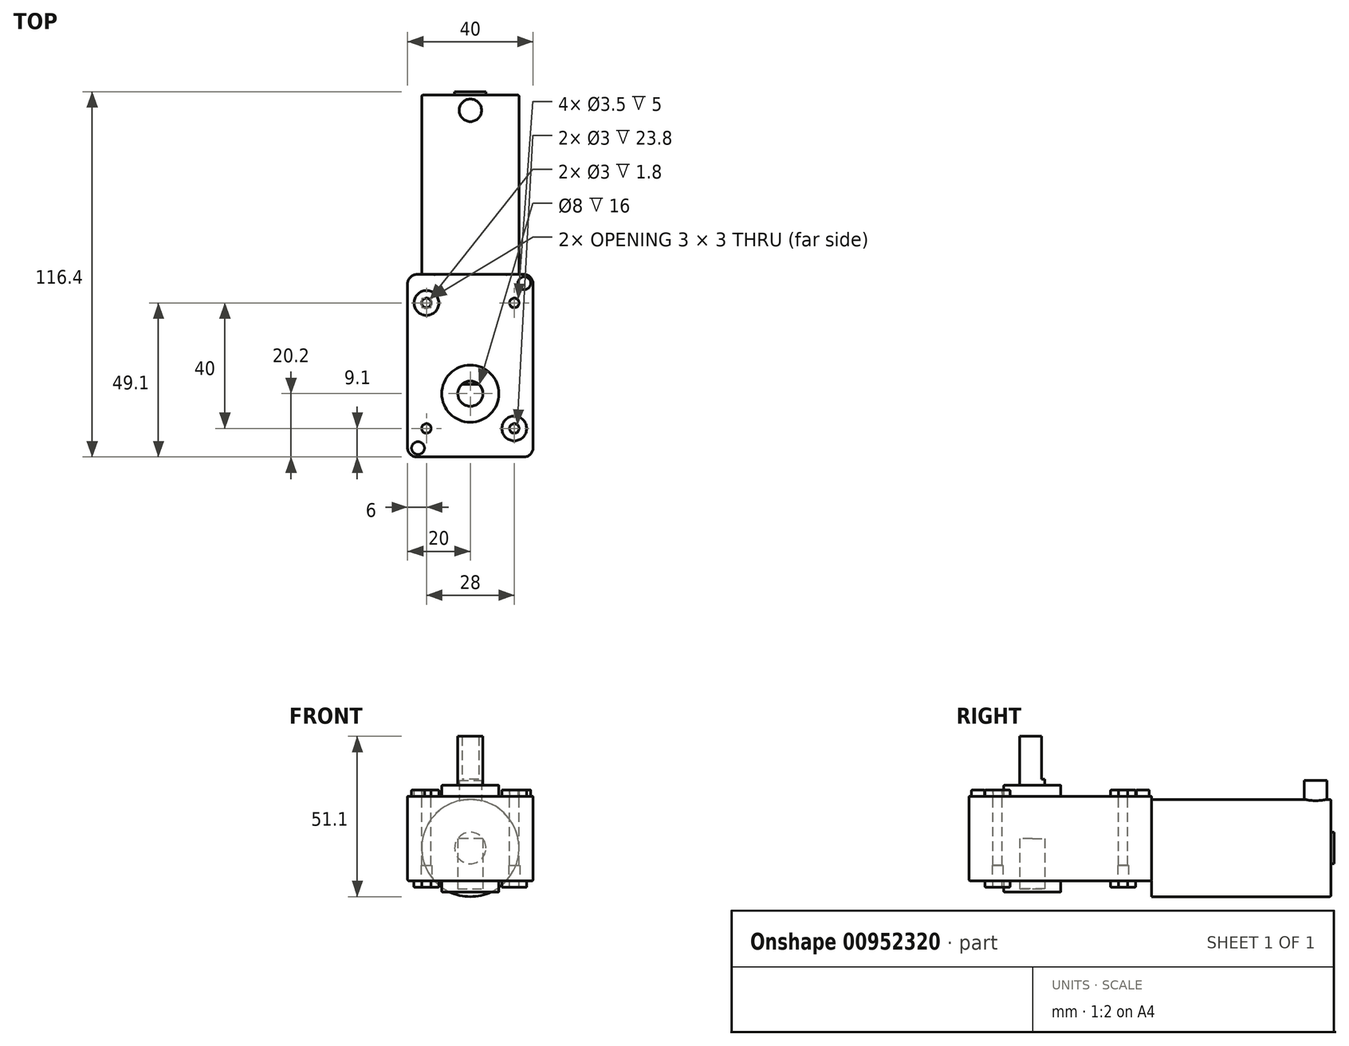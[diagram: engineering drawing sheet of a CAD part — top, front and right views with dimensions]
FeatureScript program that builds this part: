
annotation { "Feature Type Name" : "Feature", "Feature Type Description" : "" }
export const myFeature = defineFeature(function(context is Context, id is Id, definition is map)
    precondition{}
    {
        {
            var Q0;
            Q0=qCreatedBy(makeId("Top.planeOp"),FACE);
            var sketch = newSketch(context, id + "F0", { "sketchPlane" : qUnion([Q0])});
            skLineSegment(sketch, "E0.bottom", {"start": v(20, -29.1) * mm, "end": v(-20, -29.1) * mm});
            skLineSegment(sketch, "E0.top", {"start": v(20, 29.1) * mm, "end": v(-20, 29.1) * mm});
            skLineSegment(sketch, "E0.left", {"start": v(20, -29.1) * mm, "end": v(20, 29.1) * mm});
            skLineSegment(sketch, "E0.right", {"start": v(-20, -29.1) * mm, "end": v(-20, 29.1) * mm});
            skPoint(sketch, "E0.middle", {"position": v(0, 0) * mm});
            skCircle(sketch, "E1", {"center": v(0, -8.9) * mm, "radius": 4 * mm});
            skCircle(sketch, "E2", {"center": v(0, -8.9) * mm, "radius": 9.1 * mm});
            skSolve(sketch);
        }
        {
            var Q0;
            Q0=qSketchRegion(id+"F0",true);
            extrude(context, id + "F1", {"entities" : qUnion([Q0]), "depth" : 27 * mm, "offsetDistance" : 25 * mm, "symmetric" : true});
        }
        {
            var Q0;
            Q0=makeQuery(id+"F0.imprint","IMPRINT",FACE,{"disambiguationData":[TD([[makeQuery(id+"F0.imprint","IMPRINT",EDGE,{"derivedFrom":sQuery(id+"F0.wireOp",EDGE,"E1")}),-1.0]])]});
            extrude(context, id + "F2", {"entities" : qUnion([Q0]), "operationType" : NewBodyOperationType.ADD, "depth" : 34 * mm, "offsetDistance" : 25 * mm, "symmetric" : true});
        }
        {
            var Q0;
            Q0=makeQuery(id+"F6.imprint","IMPRINT",FACE,{"disambiguationData":[TD([[makeQuery(id+"F6.imprint","IMPRINT",EDGE,{"derivedFrom":sQuery(id+"F6.wireOp",EDGE,"KXEyg77E-2VgL-bzDm-OMNw-jEKFs803UJ2D")}),1.0]])]});
            var Q1;
            Q1=makeQuery(id+"F0.imprint","IMPRINT",FACE,{"disambiguationData":[TD([[makeQuery(id+"F0.imprint","IMPRINT",EDGE,{"derivedFrom":sQuery(id+"F0.wireOp",EDGE,"E1")}),1.0]])]});
            extrude(context, id + "F3", {"entities" : qUnion([Q0, Q1]), "operationType" : NewBodyOperationType.ADD, "depth" : 32.6 * mm, "offsetDistance" : 25 * mm});
        }
        {
            var Q0;
            Q0=makeQuery(id+"F1.opExtrude","SWEPT_FACE",FACE,{"disambiguationData":[OSD([sQuery(id+"F0.wireOp",EDGE,"E0.top")])]});
            var sketch = newSketch(context, id + "F4", { "sketchPlane" : qUnion([Q0])});
            skCircle(sketch, "E3", {"center": v(0, -3) * mm, "radius": 15.5 * mm});
            skSolve(sketch);
        }
        {
            var Q0;
            {var subQ0=sQuery(id+"F4.wireOp",EDGE,"E3");var subQ1=makeQuery(id+"F1.opExtrude","CAP_EDGE",EDGE,{"disambiguationData":[OSD([sQuery(id+"F0.wireOp",EDGE,"E0.top")])],"isStart":true});var subQ2=makeQuery(id+"F4.imprint","INTERSECT",VERTEX,{"disambiguationData":[OD(0.0)],"derivedFrom":[subQ1,subQ0]});Q0=makeQuery(id+"F4.imprint","IMPRINT",FACE,{"disambiguationData":[TD([[makeQuery(id+"F4.imprint","IMPRINT",EDGE,{"disambiguationData":[TD([[subQ2,-1.0]])],"derivedFrom":subQ0}),1.0]])]});}
            var Q1;
            {var subQ0=sQuery(id+"F4.wireOp",EDGE,"E3");var subQ1=sQuery(id+"F0.wireOp",EDGE,"E0.top");var subQ2=makeQuery(id+"F1.opExtrude","CAP_EDGE",EDGE,{"disambiguationData":[OSD([subQ1])],"isStart":true});var subQ3=makeQuery(id+"F4.imprint","INTERSECT",VERTEX,{"disambiguationData":[OD(0.0)],"derivedFrom":[subQ2,subQ0]});Q1=makeQuery(id+"F4.imprint","IMPRINT",FACE,{"disambiguationData":[TD([[makeQuery(id+"F4.imprint","IMPRINT",EDGE,{"disambiguationData":[TD([[subQ3,1.0]])],"derivedFrom":subQ0}),1.0]])]});}
            extrude(context, id + "F5", {"entities" : qUnion([Q0, Q1]), "operationType" : NewBodyOperationType.ADD, "depth" : 57.2 * mm, "offsetDistance" : 25 * mm});
        }
        {
            var Q0;
            Q0=makeQuery(id+"F1.opExtrude","CAP_FACE",FACE,{"disambiguationData":[OSD([sQuery(id+"F0.wireOp",EDGE,"E0.bottom"),sQuery(id+"F0.wireOp",EDGE,"E0.top"),sQuery(id+"F0.wireOp",EDGE,"E0.left"),sQuery(id+"F0.wireOp",EDGE,"E0.right")])],"isStart":false});
            var sketch = newSketch(context, id + "F6", { "sketchPlane" : qUnion([Q0])});
            skCircle(sketch, "E4", {"center": v(-14, 20) * mm, "radius": 1.5 * mm});
            skCircle(sketch, "E5.MirrorC", {"center": v(14, 20) * mm, "radius": 1.5 * mm});
            skCircle(sketch, "E6.MirrorC", {"center": v(-14, -20) * mm, "radius": 1.5 * mm});
            skCircle(sketch, "E7.MirrorC", {"center": v(14, -20) * mm, "radius": 1.5 * mm});
            skCircle(sketch, "E8", {"center": v(-14, 20) * mm, "radius": 3.95 * mm});
            skArc(sketch, "E9.MirrorC", {"start": v(11.3, 22.89) * mm, "mid": v(16.89, 22.7) * mm, "end": v(16.7, 17.11) * mm});
            skCircle(sketch, "E10.MirrorC", {"center": v(-14, -20) * mm, "radius": 3.95 * mm});
            skCircle(sketch, "E11.MirrorC", {"center": v(14, -20) * mm, "radius": 3.95 * mm});
            skCircle(sketch, "E12", {"center": v(0, -8.9) * mm, "radius": 6.39 * mm});
            skArc(sketch, "E13", {"start": v(4.87, 16.88) * mm, "mid": v(4.68, 11.3) * mm, "end": v(10.26, 11.1) * mm});
            skLineSegment(sketch, "E14", {"start": v(16.7, 17.11) * mm, "end": v(10.26, 11.1) * mm});
            skLineSegment(sketch, "E15.MirrorCS", {"start": v(11.3, 22.89) * mm, "end": v(4.87, 16.88) * mm});
            skCircle(sketch, "E16", {"center": v(17.2, 26.3) * mm, "radius": 2.05 * mm});
            skLineSegment(sketch, "E17", {"start": v(20, 0) * mm, "end": v(19.1, 0) * mm});
            skLineSegment(sketch, "E18", {"start": v(0, -29.1) * mm, "end": v(0, -27.97) * mm});
            skCircle(sketch, "E19.MirrorC", {"center": v(16.67, -26.24) * mm, "radius": 2.05 * mm});
            skCircle(sketch, "E20.MirrorC", {"center": v(-16.67, -26.24) * mm, "radius": 2.05 * mm});
            skCircle(sketch, "E21.MirrorC", {"center": v(-17.2, 26.3) * mm, "radius": 2.05 * mm});
            skSolve(sketch);
        }
        {
            var Q0;
            Q0=makeQuery(id+"F3.opExtrude","CAP_FACE",FACE,{"disambiguationData":[OSD([sQuery(id+"F0.wireOp",EDGE,"E1")])],"isStart":false});
            var sketch = newSketch(context, id + "F7", { "sketchPlane" : qUnion([Q0])});
            skLineSegment(sketch, "E22.bottom", {"start": v(5, -5.9) * mm, "end": v(-5, -5.9) * mm});
            skLineSegment(sketch, "E22.top", {"start": v(5, -3.9) * mm, "end": v(-5, -3.9) * mm});
            skLineSegment(sketch, "E22.left", {"start": v(5, -5.9) * mm, "end": v(5, -3.9) * mm});
            skLineSegment(sketch, "E22.right", {"start": v(-5, -5.9) * mm, "end": v(-5, -3.9) * mm});
            skPoint(sketch, "E22.middle", {"position": v(0, -4.9) * mm});
            skCircle(sketch, "E23", {"center": v(0, -8.9) * mm, "radius": 4 * mm});
            skSolve(sketch);
        }
        {
            var Q0;
            Q0=makeQuery(id+"F7.imprint","IMPRINT",FACE,{"disambiguationData":[TD([[makeQuery(id+"F7.imprint","IMPRINT",EDGE,{"derivedFrom":sQuery(id+"F7.wireOp",EDGE,"E22.top")}),1.0]])]});
            var Q1;
            {var subQ0=sQuery(id+"F7.wireOp",EDGE,"E23");var subQ1=sQuery(id+"F7.wireOp",EDGE,"E22.bottom");var subQ2=makeQuery(id+"F7.imprint","INTERSECT",VERTEX,{"disambiguationData":[OD(0.0)],"derivedFrom":[subQ1,subQ0]});Q1=makeQuery(id+"F7.imprint","IMPRINT",FACE,{"disambiguationData":[TD([[makeQuery(id+"F7.imprint","IMPRINT",EDGE,{"disambiguationData":[TD([[subQ2,-1.0]])],"derivedFrom":subQ1}),-1.0]])]});}
            extrude(context, id + "F8", {"entities" : qUnion([Q0, Q1]), "operationType" : NewBodyOperationType.REMOVE, "oppositeDirection" : true, "depth" : 13.7 * mm, "offsetDistance" : 25 * mm});
        }
        {
            var Q0;
            Q0=makeQuery(id+"F6.imprint","IMPRINT",FACE,{"disambiguationData":[TD([[makeQuery(id+"F6.imprint","IMPRINT",EDGE,{"derivedFrom":sQuery(id+"F6.wireOp",EDGE,"E5.MirrorC")}),1.0]])]});
            var Q1;
            Q1=makeQuery(id+"F6.imprint","IMPRINT",FACE,{"disambiguationData":[TD([[makeQuery(id+"F6.imprint","IMPRINT",EDGE,{"derivedFrom":sQuery(id+"F6.wireOp",EDGE,"E6.MirrorC")}),1.0]])]});
            var Q2;
            Q2=makeQuery(id+"F6.imprint","IMPRINT",FACE,{"disambiguationData":[TD([[makeQuery(id+"F6.imprint","IMPRINT",EDGE,{"derivedFrom":sQuery(id+"F6.wireOp",EDGE,"E7.MirrorC")}),-1.0]])]});
            var Q3;
            Q3=makeQuery(id+"F6.imprint","IMPRINT",FACE,{"disambiguationData":[TD([[makeQuery(id+"F6.imprint","IMPRINT",EDGE,{"derivedFrom":sQuery(id+"F6.wireOp",EDGE,"E4")}),-1.0]])]});
            extrude(context, id + "F9", {"entities" : qUnion([Q0, Q1, Q2, Q3]), "operationType" : NewBodyOperationType.ADD, "oppositeDirection" : true, "depth" : 29 * mm, "offsetDistance" : 25 * mm});
        }
        {
            var Q0;
            Q0=makeQuery(id+"F6.imprint","IMPRINT",FACE,{"disambiguationData":[TD([[makeQuery(id+"F6.imprint","IMPRINT",EDGE,{"derivedFrom":sQuery(id+"F6.wireOp",EDGE,"E4")}),-1.0]])]});
            var Q1;
            Q1=makeQuery(id+"F6.imprint","IMPRINT",FACE,{"disambiguationData":[TD([[makeQuery(id+"F6.imprint","IMPRINT",EDGE,{"derivedFrom":sQuery(id+"F6.wireOp",EDGE,"E5.MirrorC")}),1.0]])]});
            var Q2;
            Q2=makeQuery(id+"F6.imprint","IMPRINT",FACE,{"disambiguationData":[TD([[makeQuery(id+"F6.imprint","IMPRINT",EDGE,{"derivedFrom":sQuery(id+"F6.wireOp",EDGE,"E6.MirrorC")}),1.0]])]});
            var Q3;
            Q3=makeQuery(id+"F6.imprint","IMPRINT",FACE,{"disambiguationData":[TD([[makeQuery(id+"F6.imprint","IMPRINT",EDGE,{"derivedFrom":sQuery(id+"F6.wireOp",EDGE,"E7.MirrorC")}),-1.0]])]});
            var Q4;
            Q4=makeQuery(id+"F6.imprint","IMPRINT",FACE,{"disambiguationData":[TD([[makeQuery(id+"F6.imprint","IMPRINT",EDGE,{"derivedFrom":sQuery(id+"F6.wireOp",EDGE,"E16")}),1.0]])]});
            var Q5;
            Q5=makeQuery(id+"F6.imprint","IMPRINT",FACE,{"disambiguationData":[TD([[makeQuery(id+"F6.imprint","IMPRINT",EDGE,{"derivedFrom":sQuery(id+"F6.wireOp",EDGE,"E21.MirrorC")}),-1.0]])]});
            var Q6;
            Q6=makeQuery(id+"F6.imprint","IMPRINT",FACE,{"disambiguationData":[TD([[makeQuery(id+"F6.imprint","IMPRINT",EDGE,{"derivedFrom":sQuery(id+"F6.wireOp",EDGE,"E20.MirrorC")}),1.0]])]});
            var Q7;
            Q7=makeQuery(id+"F6.imprint","IMPRINT",FACE,{"disambiguationData":[TD([[makeQuery(id+"F6.imprint","IMPRINT",EDGE,{"derivedFrom":sQuery(id+"F6.wireOp",EDGE,"E19.MirrorC")}),-1.0]])]});
            extrude(context, id + "F10", {"entities" : qUnion([Q0, Q1, Q2, Q3, Q4, Q5, Q6, Q7]), "operationType" : NewBodyOperationType.ADD, "depth" : 2 * mm, "offsetDistance" : 25 * mm});
        }
        {
            var Q0;
            Q0=makeQuery(id+"F10.boolean.opBoolean","SPLIT",FACE,{"disambiguationData":[TD([makeQuery(id+"F10.opExtrude","SWEPT_FACE",FACE,{"disambiguationData":[OSD([sQuery(id+"F6.wireOp",EDGE,"E4")])]})])],"derivedFrom":makeQuery(id+"F1.opExtrude","CAP_FACE",FACE,{"disambiguationData":[OSD([sQuery(id+"F0.wireOp",EDGE,"E0.bottom"),sQuery(id+"F0.wireOp",EDGE,"E0.top"),sQuery(id+"F0.wireOp",EDGE,"E0.left"),sQuery(id+"F0.wireOp",EDGE,"E0.right"),sQuery(id+"F0.wireOp",EDGE,"E2")])],"isStart":false})});
            var Q1;
            Q1=makeQuery(id+"F10.boolean.opBoolean","SPLIT",FACE,{"disambiguationData":[TD([makeQuery(id+"F10.opExtrude","SWEPT_FACE",FACE,{"disambiguationData":[OSD([sQuery(id+"F6.wireOp",EDGE,"E5.MirrorC")])]})])],"derivedFrom":makeQuery(id+"F1.opExtrude","CAP_FACE",FACE,{"disambiguationData":[OSD([sQuery(id+"F0.wireOp",EDGE,"E0.bottom"),sQuery(id+"F0.wireOp",EDGE,"E0.top"),sQuery(id+"F0.wireOp",EDGE,"E0.left"),sQuery(id+"F0.wireOp",EDGE,"E0.right"),sQuery(id+"F0.wireOp",EDGE,"E2")])],"isStart":false})});
            var Q2;
            Q2=makeQuery(id+"F10.boolean.opBoolean","SPLIT",FACE,{"disambiguationData":[TD([makeQuery(id+"F10.opExtrude","SWEPT_FACE",FACE,{"disambiguationData":[OSD([sQuery(id+"F6.wireOp",EDGE,"E6.MirrorC")])]})])],"derivedFrom":makeQuery(id+"F1.opExtrude","CAP_FACE",FACE,{"disambiguationData":[OSD([sQuery(id+"F0.wireOp",EDGE,"E0.bottom"),sQuery(id+"F0.wireOp",EDGE,"E0.top"),sQuery(id+"F0.wireOp",EDGE,"E0.left"),sQuery(id+"F0.wireOp",EDGE,"E0.right"),sQuery(id+"F0.wireOp",EDGE,"E2")])],"isStart":false})});
            var Q3;
            Q3=makeQuery(id+"F10.boolean.opBoolean","SPLIT",FACE,{"disambiguationData":[TD([makeQuery(id+"F10.opExtrude","SWEPT_FACE",FACE,{"disambiguationData":[OSD([sQuery(id+"F6.wireOp",EDGE,"E7.MirrorC")])]})])],"derivedFrom":makeQuery(id+"F1.opExtrude","CAP_FACE",FACE,{"disambiguationData":[OSD([sQuery(id+"F0.wireOp",EDGE,"E0.bottom"),sQuery(id+"F0.wireOp",EDGE,"E0.top"),sQuery(id+"F0.wireOp",EDGE,"E0.left"),sQuery(id+"F0.wireOp",EDGE,"E0.right"),sQuery(id+"F0.wireOp",EDGE,"E2")])],"isStart":false})});
            extrude(context, id + "F11", {"entities" : qUnion([Q0, Q1, Q2, Q3]), "operationType" : NewBodyOperationType.REMOVE, "endBound" : BoundingType.THROUGH_ALL, "oppositeDirection" : true, "depth" : 25 * mm, "offsetDistance" : 25 * mm});
        }
        {
            var Q0;
            Q0=makeQuery(id+"F5.opExtrude","CAP_FACE",FACE,{"disambiguationData":[OSD([sQuery(id+"F4.wireOp",EDGE,"E3")])],"isStart":false});
            var sketch = newSketch(context, id + "F12", { "sketchPlane" : qUnion([Q0])});
            skCircle(sketch, "E24", {"center": v(0, -3) * mm, "radius": 5 * mm});
            skSolve(sketch);
        }
        {
            var Q0;
            Q0=qSketchRegion(id+"F12",true);
            extrude(context, id + "F13", {"entities" : qUnion([Q0]), "operationType" : NewBodyOperationType.ADD, "depth" : 1 * mm, "offsetDistance" : 25 * mm});
        }
        {
            var Q0;
            {var subQ0=sQuery(id+"F0.wireOp",EDGE,"E0.left");var subQ1=sQuery(id+"F0.wireOp",EDGE,"E0.top");var subQ2=sQuery(id+"F0.wireOp",EDGE,"E0.right");var subQ3=sQuery(id+"F0.wireOp",EDGE,"E0.bottom");var subQ4=sQuery(id+"F0.wireOp",EDGE,"E2");Q0=makeQuery(id+"F10.boolean.opBoolean","SPLIT",FACE,{"disambiguationData":[TD([makeQuery(id+"F1.opExtrude","SWEPT_FACE",FACE,{"disambiguationData":[OSD([subQ3])]})])],"derivedFrom":makeQuery(id+"F1.opExtrude","CAP_FACE",FACE,{"disambiguationData":[OSD([subQ3,subQ1,subQ0,subQ2,subQ4])],"isStart":false})});}
            var sketch = newSketch(context, id + "F14", { "sketchPlane" : qUnion([Q0])});
            skCircle(sketch, "E25", {"center": v(0, 81.39) * mm, "radius": 3.59 * mm});
            skSolve(sketch);
        }
        {
            var Q0;
            Q0=makeQuery(id+"F14.imprint","IMPRINT",FACE,{"disambiguationData":[TD([[makeQuery(id+"F14.imprint","IMPRINT",EDGE,{"derivedFrom":sQuery(id+"F14.wireOp",EDGE,"E25")}),1.0]])]});
            extrude(context, id + "F15", {"entities" : qUnion([Q0]), "operationType" : NewBodyOperationType.ADD, "depth" : 10 * mm, "offsetDistance" : 25 * mm, "symmetric" : true});
        }
        {
            var Q0;
            Q0=makeQuery(id+"F1.opExtrude","SWEPT_EDGE",EDGE,{"disambiguationData":[OSD([sQuery(id+"F0.wireOp",EDGE,"E0.top"),sQuery(id+"F0.wireOp",EDGE,"E0.right")])]});
            var Q1;
            Q1=makeQuery(id+"F1.opExtrude","SWEPT_EDGE",EDGE,{"disambiguationData":[OSD([sQuery(id+"F0.wireOp",EDGE,"E0.top"),sQuery(id+"F0.wireOp",EDGE,"E0.left")])]});
            var Q2;
            Q2=makeQuery(id+"F1.opExtrude","SWEPT_EDGE",EDGE,{"disambiguationData":[OSD([sQuery(id+"F0.wireOp",EDGE,"E0.bottom"),sQuery(id+"F0.wireOp",EDGE,"E0.left")])]});
            var Q3;
            Q3=makeQuery(id+"F1.opExtrude","SWEPT_EDGE",EDGE,{"disambiguationData":[OSD([sQuery(id+"F0.wireOp",EDGE,"E0.bottom"),sQuery(id+"F0.wireOp",EDGE,"E0.right")])]});
            fillet(context, id + "F16", {"entities" : qUnion([Q0, Q1, Q2, Q3]), "radius" : 3 * mm, "tangentPropagation" : true, "defaultsChanged" : true, "vertexSettings" : [], "allowEdgeOverflow" : false});
        }
        {
            var Q0;
            {var subQ0=sQuery(id+"F0.wireOp",EDGE,"E0.left");var subQ1=sQuery(id+"F0.wireOp",EDGE,"E0.top");var subQ2=sQuery(id+"F0.wireOp",EDGE,"E0.right");var subQ3=sQuery(id+"F0.wireOp",EDGE,"E0.bottom");var subQ4=sQuery(id+"F0.wireOp",EDGE,"E2");Q0=makeQuery(id+"F10.boolean.opBoolean","SPLIT",FACE,{"disambiguationData":[TD([makeQuery(id+"F1.opExtrude","SWEPT_FACE",FACE,{"disambiguationData":[OSD([subQ3])]})])],"derivedFrom":makeQuery(id+"F1.opExtrude","CAP_FACE",FACE,{"disambiguationData":[OSD([subQ3,subQ1,subQ0,subQ2,subQ4])],"isStart":false})});}
            var Q1;
            Q1=makeQuery(id+"F10.opExtrude","CAP_FACE",FACE,{"disambiguationData":[OSD([sQuery(id+"F6.wireOp",EDGE,"E5.MirrorC"),sQuery(id+"F6.wireOp",EDGE,"E9.MirrorC"),sQuery(id+"F6.wireOp",EDGE,"E13"),sQuery(id+"F6.wireOp",EDGE,"E14"),sQuery(id+"F6.wireOp",EDGE,"E15.MirrorCS")])],"isStart":false});
            var Q2;
            Q2=makeQuery(id+"F10.opExtrude","CAP_FACE",FACE,{"disambiguationData":[OSD([sQuery(id+"F6.wireOp",EDGE,"E16")])],"isStart":false});
            var Q3;
            Q3=makeQuery(id+"F10.opExtrude","CAP_EDGE",EDGE,{"disambiguationData":[OSD([sQuery(id+"F6.wireOp",EDGE,"E21.MirrorC")])],"isStart":false});
            var Q4;
            Q4=makeQuery(id+"F10.opExtrude","CAP_FACE",FACE,{"disambiguationData":[OSD([sQuery(id+"F6.wireOp",EDGE,"E4"),sQuery(id+"F6.wireOp",EDGE,"E8")])],"isStart":false});
            var Q5;
            Q5=makeQuery(id+"F10.opExtrude","CAP_FACE",FACE,{"disambiguationData":[OSD([sQuery(id+"F6.wireOp",EDGE,"E6.MirrorC"),sQuery(id+"F6.wireOp",EDGE,"E10.MirrorC")])],"isStart":false});
            var Q6;
            Q6=makeQuery(id+"F10.opExtrude","CAP_FACE",FACE,{"disambiguationData":[OSD([sQuery(id+"F6.wireOp",EDGE,"E20.MirrorC")])],"isStart":false});
            var Q7;
            Q7=makeQuery(id+"F10.opExtrude","CAP_EDGE",EDGE,{"disambiguationData":[OSD([sQuery(id+"F6.wireOp",EDGE,"E19.MirrorC")])],"isStart":false});
            var Q8;
            Q8=makeQuery(id+"F10.opExtrude","CAP_FACE",FACE,{"disambiguationData":[OSD([sQuery(id+"F6.wireOp",EDGE,"E7.MirrorC"),sQuery(id+"F6.wireOp",EDGE,"E11.MirrorC")])],"isStart":false});
            var Q9;
            Q9=makeQuery(id+"F2.opExtrude","CAP_FACE",FACE,{"disambiguationData":[OSD([sQuery(id+"F0.wireOp",EDGE,"E1"),sQuery(id+"F0.wireOp",EDGE,"E2")])],"isStart":false});
            var Q10;
            Q10=makeQuery(id+"F9.opExtrude","CAP_FACE",FACE,{"disambiguationData":[OSD([sQuery(id+"F6.wireOp",EDGE,"E4"),sQuery(id+"F6.wireOp",EDGE,"E8")])],"isStart":false});
            var Q11;
            Q11=makeQuery(id+"F9.opExtrude","CAP_FACE",FACE,{"disambiguationData":[OSD([sQuery(id+"F6.wireOp",EDGE,"E5.MirrorC"),sQuery(id+"F6.wireOp",EDGE,"E9.MirrorC"),sQuery(id+"F6.wireOp",EDGE,"E13"),sQuery(id+"F6.wireOp",EDGE,"E14"),sQuery(id+"F6.wireOp",EDGE,"E15.MirrorCS")])],"isStart":false});
            var Q12;
            Q12=makeQuery(id+"F9.opExtrude","CAP_FACE",FACE,{"disambiguationData":[OSD([sQuery(id+"F6.wireOp",EDGE,"E7.MirrorC"),sQuery(id+"F6.wireOp",EDGE,"E11.MirrorC")])],"isStart":false});
            var Q13;
            Q13=makeQuery(id+"F9.opExtrude","CAP_FACE",FACE,{"disambiguationData":[OSD([sQuery(id+"F6.wireOp",EDGE,"E6.MirrorC"),sQuery(id+"F6.wireOp",EDGE,"E10.MirrorC")])],"isStart":false});
            var Q14;
            Q14=makeQuery(id+"F2.opExtrude","CAP_FACE",FACE,{"disambiguationData":[OSD([sQuery(id+"F0.wireOp",EDGE,"E1"),sQuery(id+"F0.wireOp",EDGE,"E2")])],"isStart":true});
            fillet(context, id + "F17", {"entities" : qUnion([Q0, Q1, Q2, Q3, Q4, Q5, Q6, Q7, Q8, Q9, Q10, Q11, Q12, Q13, Q14]), "radius" : 0.2 * mm, "tangentPropagation" : true, "defaultsChanged" : false, "vertexSettings" : [], "allowEdgeOverflow" : false});
        }
        {
            var Q0;
            Q0=makeQuery(id+"F1.opExtrude","CAP_EDGE",EDGE,{"disambiguationData":[OSD([sQuery(id+"F0.wireOp",EDGE,"E0.left")])],"isStart":true});
            var Q1;
            Q1=makeQuery(id+"F5.opExtrude","CAP_EDGE",EDGE,{"disambiguationData":[OSD([sQuery(id+"F4.wireOp",EDGE,"E3")])],"isStart":false});
            var Q2;
            Q2=makeQuery(id+"F2.opExtrude","CAP_EDGE",EDGE,{"disambiguationData":[OSD([sQuery(id+"F0.wireOp",EDGE,"E2")])],"isStart":false});
            var Q3;
            Q3=makeQuery(id+"F2.opExtrude","CAP_EDGE",EDGE,{"disambiguationData":[OSD([sQuery(id+"F0.wireOp",EDGE,"E2")])],"isStart":true});
            var Q4;
            Q4=makeQuery(id+"F1.opExtrude","CAP_EDGE",EDGE,{"disambiguationData":[OSD([sQuery(id+"F0.wireOp",EDGE,"E2")])],"isStart":true});
            fillet(context, id + "F18", {"entities" : qUnion([Q0, Q1, Q2, Q3, Q4]), "radius" : 0.5 * mm, "tangentPropagation" : true, "allowEdgeOverflow" : false});
        }
        {
            var Q0;
            Q0=makeQuery(id+"F2.opExtrude","CAP_FACE",FACE,{"disambiguationData":[OSD([sQuery(id+"F0.wireOp",EDGE,"E1"),sQuery(id+"F0.wireOp",EDGE,"E2")])],"isStart":true});
            var sketch = newSketch(context, id + "F19", { "sketchPlane" : qUnion([Q0])});
            skCircle(sketch, "E26", {"center": v(0, 8.85) * mm, "radius": 5 * mm});
            skSolve(sketch);
        }
        {
            var Q0;
            Q0 = qSketchRegion(id + "F19", true);
            extrude(context, id + "F20", {"entities" : qUnion([Q0]), "operationType" : NewBodyOperationType.ADD, "oppositeDirection" : true, "depth" : 1 * mm, "offsetDistance" : 25 * mm});
        }
        {
            var Q0;
            {var subQ1=sQuery(id+"F0.wireOp",EDGE,"E2");var subQ2=sQuery(id+"F0.wireOp",EDGE,"E0.bottom");var subQ3=sQuery(id+"F0.wireOp",EDGE,"E0.right");var subQ4=sQuery(id+"F0.wireOp",EDGE,"E0.left");var subQ5=sQuery(id+"F0.wireOp",EDGE,"E0.top");Q0=makeQuery(id+"F9.boolean.opBoolean","SPLIT",FACE,{"disambiguationData":[TD([makeQuery(id+"F1.opExtrude","SWEPT_FACE",FACE,{"disambiguationData":[OSD([subQ2])]})])],"derivedFrom":makeQuery(id+"F1.opExtrude","CAP_FACE",FACE,{"disambiguationData":[OSD([subQ2,subQ5,subQ4,subQ3,subQ1])],"isStart":true})});}
            var sketch = newSketch(context, id + "F21", { "sketchPlane" : qUnion([Q0])});
            skCircle(sketch, "E27", {"center": v(-14, 20) * mm, "radius": 1.75 * mm});
            skLineSegment(sketch, "E28", {"start": v(0, 28.6) * mm, "end": v(0, 27.18) * mm});
            skLineSegment(sketch, "E29", {"start": v(-19.5, 0) * mm, "end": v(-15.4, 0) * mm});
            skCircle(sketch, "E30.MirrorC", {"center": v(-14, -20) * mm, "radius": 1.75 * mm});
            skCircle(sketch, "E31.MirrorC", {"center": v(14, 20) * mm, "radius": 1.75 * mm});
            skCircle(sketch, "E32.MirrorC", {"center": v(14, -20) * mm, "radius": 1.75 * mm});
            skSolve(sketch);
        }
        {
            var Q0;
            Q0 = qSketchRegion(id + "F21", true);
            extrude(context, id + "F22", {"entities" : qUnion([Q0]), "operationType" : NewBodyOperationType.REMOVE, "oppositeDirection" : true, "depth" : 5 * mm, "offsetDistance" : 25 * mm});
        }
    });
